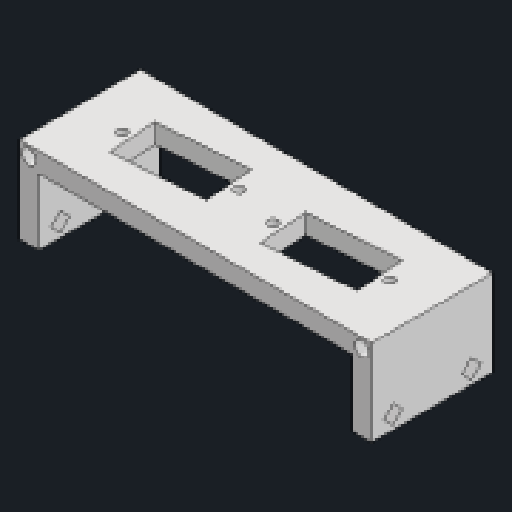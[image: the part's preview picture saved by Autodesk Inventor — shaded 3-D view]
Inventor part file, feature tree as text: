
AUTODESK INVENTOR PART (.ipt)
format: ipt  version: 2023.2 (Build 272271030, 271C)  size: 180,224 bytes
history: native  units: mm
features: sketch x5, extrude x3, projected_geometry x3, hole x2, other x2, mirror x1
ambient origin geometry x8: Origin, YZ Plane, XZ Plane, XY Plane, X Axis, Y Axis, Z Axis, Center Point
bodies: Solid1 (feature_tree)
feature tree (16):
  extrude  "Extrusion1"  Depth=80.0mm
  extrude  "Extrusion2"  Depth=31.0mm TaperAngle=0.0deg
  hole  "Hole1"  [1 undecoded]
  extrude  "Extrusion3"  Depth=10.0mm
  other  "Work Axis1"
  other  "Work Axis2"
  hole  "Hole2"  [1 undecoded]
  mirror  "Mirror1"
  sketch  "Sketch1"  dims[d0=5.0mm d1=80.0mm]
  sketch  "Sketch2"  dims[d2=22.0mm d3=31.0mm d4=0.0mm]
  sketch  "Sketch3"  dims[d5=3.4mm d6=20.0mm]
  projected_geometry  "Projected Loop1"
  sketch  "Sketch4"  dims[d7=18.5mm d8=10.0mm]
  projected_geometry  "Projected Loop2"
  sketch  "Sketch5"  dims[d9=0.0mm d10=0.0mm d11=5.0mm d12=12.0mm d13=27.8mm d14=19.05mm d15=19.05mm d16=31.0mm d17=11.61895mm d18=5.809475mm d19=3.0mm d20=2.5mm d21=6.0mm d22=4.5mm d23=5.8mm d24=90.0deg d25=8.0mm d26=20.594885mm d27=23.0mm d28=12.5mm d29=0.0mm d30=0.0mm d31=2.5mm d32=2.5mm d33=2.5mm d34=3.7mm d35=6.0mm d36=4.0mm d37=2.0mm d38=90.0deg d39=3.5mm d40=0.0mm]
  projected_geometry  "Projected Loop3"
note: 2 required parameter values undecoded (feature->parameter linkage not recoverable at this tier; creation-order binding heuristic only, values carry confidence <= 0.55)
